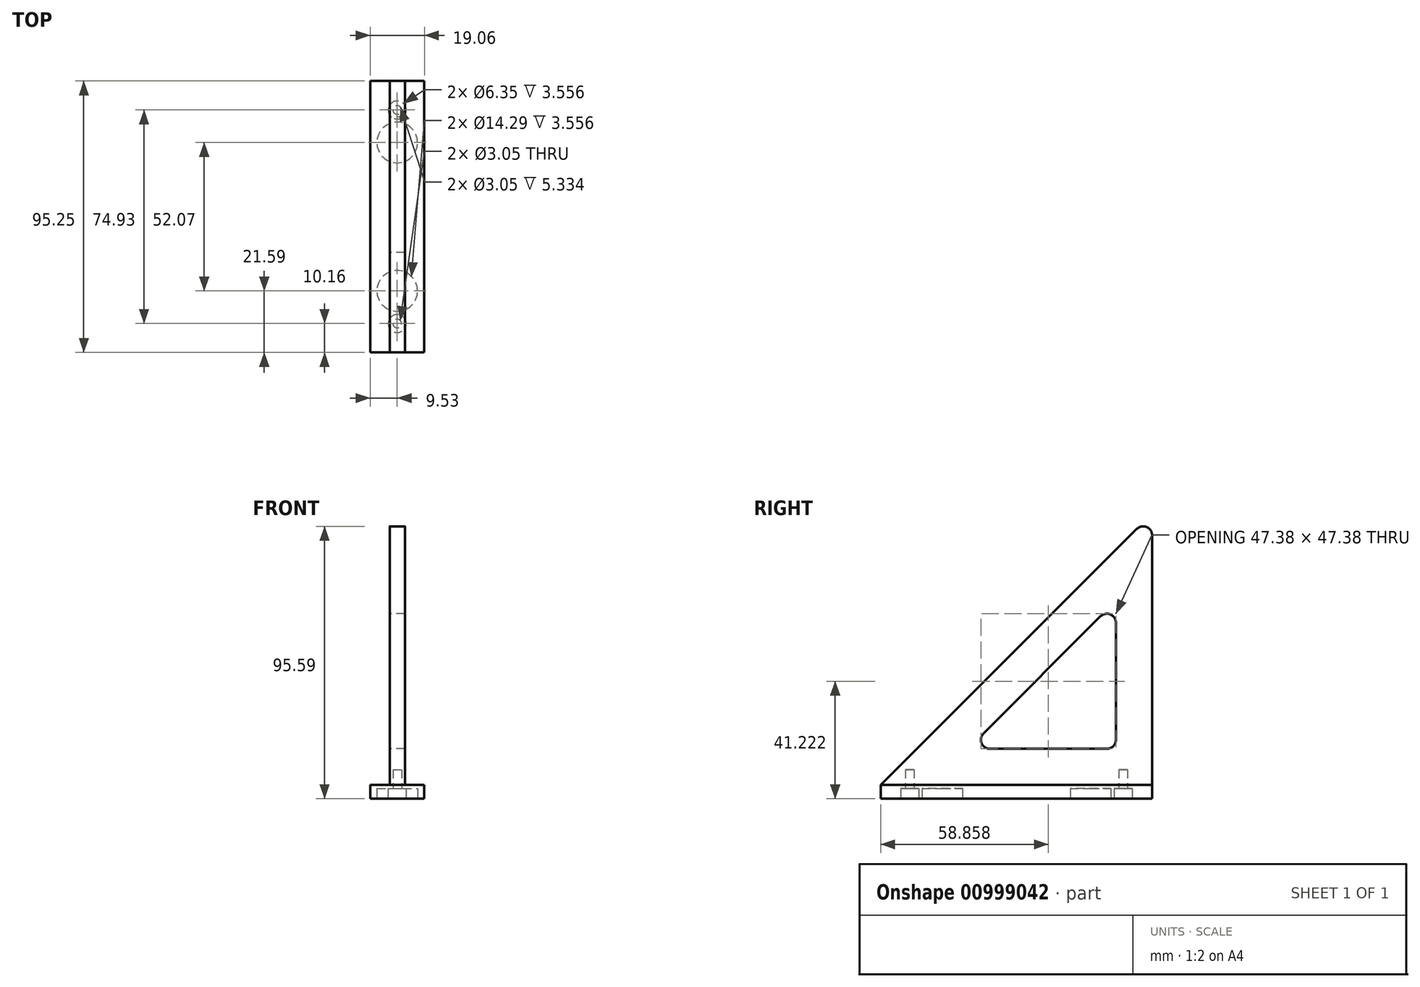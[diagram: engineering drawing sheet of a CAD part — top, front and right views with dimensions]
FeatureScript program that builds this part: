
annotation { "Feature Type Name" : "Feature", "Feature Type Description" : "" }
export const myFeature = defineFeature(function(context is Context, id is Id, definition is map)
    precondition{}
    {
        {
            var Q0;
            Q0=qCreatedBy(makeId("Right.planeOp"),FACE);
            var sketch = newSketch(context, id + "F0", { "sketchPlane" : qUnion([Q0])});
            skLineSegment(sketch, "E0", {"start": v(0, 0) * mm, "end": v(89.83, 89.83) * mm});
            skLineSegment(sketch, "E1", {"start": v(95.25, 87.58) * mm, "end": v(95.25, 0) * mm});
            skLineSegment(sketch, "E2", {"start": v(95.25, 0) * mm, "end": v(7.67, 0) * mm});
            skLineSegment(sketch, "E3.0", {"start": v(36.08, 18.12) * mm, "end": v(77.13, 59.17) * mm});
            skLineSegment(sketch, "E3.1", {"start": v(79.38, 12.7) * mm, "end": v(38.33, 12.7) * mm});
            skLineSegment(sketch, "E3.2", {"start": v(82.55, 56.92) * mm, "end": v(82.55, 15.88) * mm});
            skPoint(sketch, "E4.visualSharp", {"position": v(95.25, 95.25) * mm});
            skArc(sketch, "E4.filletArc", {"start": v(95.25, 87.58) * mm, "mid": v(93.3, 90.52) * mm, "end": v(89.83, 89.83) * mm});
            skPoint(sketch, "E5.visualSharp", {"position": v(0, 0) * mm});
            skPoint(sketch, "E6.visualSharp", {"position": v(30.66, 12.7) * mm});
            skArc(sketch, "E6.filletArc", {"start": v(36.08, 18.12) * mm, "mid": v(35.4, 14.66) * mm, "end": v(38.33, 12.7) * mm});
            skPoint(sketch, "E7.visualSharp", {"position": v(82.55, 64.59) * mm});
            skArc(sketch, "E7.filletArc", {"start": v(82.55, 56.92) * mm, "mid": v(80.6, 59.86) * mm, "end": v(77.13, 59.17) * mm});
            skPoint(sketch, "E8.visualSharp", {"position": v(82.55, 12.7) * mm});
            skArc(sketch, "E8.filletArc", {"start": v(79.38, 12.7) * mm, "mid": v(81.62, 13.63) * mm, "end": v(82.55, 15.88) * mm});
            skLineSegment(sketch, "E9", {"start": v(0, 0) * mm, "end": v(7.67, 0) * mm});
            skPoint(sketch, "E10.visualSharp", {"position": v(24.47, 24.47) * mm});
            skSolve(sketch);
        }
        {
            var Q0;
            Q0=makeQuery(id+"F0.imprint","IMPRINT",FACE,{"disambiguationData":[TD([[makeQuery(id+"F0.imprint","IMPRINT",EDGE,{"derivedFrom":sQuery(id+"F0.wireOp",EDGE,"E0")}),-1.0]])]});
            extrude(context, id + "F1", {"entities" : qUnion([Q0]), "depth" : 2.67 * mm, "offsetDistance" : 25.4 * mm, "hasSecondDirection" : true, "secondDirectionOppositeDirection" : true, "secondDirectionDepth" : 2.67 * mm});
        }
        {
            var Q0;
            Q0=qCreatedBy(makeId("Right.planeOp"),FACE);
            var sketch = newSketch(context, id + "F2", { "sketchPlane" : qUnion([Q0])});
            skLineSegment(sketch, "E11.bottom", {"start": v(95.25, 0) * mm, "end": v(0, 0) * mm});
            skLineSegment(sketch, "E11.top", {"start": v(95.25, -4.83) * mm, "end": v(0, -4.83) * mm});
            skLineSegment(sketch, "E11.left", {"start": v(95.25, -4.83) * mm, "end": v(95.25, 0) * mm});
            skLineSegment(sketch, "E11.right", {"start": v(0, -4.83) * mm, "end": v(0, 0) * mm});
            skSolve(sketch);
        }
        {
            var Q0;
            Q0 = qSketchRegion(id + "F2", true);
            extrude(context, id + "F3", {"entities" : qUnion([Q0]), "depth" : 9.52 * mm, "offsetDistance" : 25.4 * mm, "hasSecondDirection" : true, "secondDirectionOppositeDirection" : true, "secondDirectionDepth" : 9.52 * mm});
        }
        {
            var Q0;
            Q0=makeQuery(id+"F3.opExtrude","SWEPT_FACE",FACE,{"disambiguationData":[OSD([sQuery(id+"F2.wireOp",EDGE,"E11.top")])]});
            var sketch = newSketch(context, id + "F4", { "sketchPlane" : qUnion([Q0])});
            skCircle(sketch, "E12", {"center": v(0, -85.1) * mm, "radius": 3.18 * mm});
            skCircle(sketch, "E13", {"center": v(0, -10.16) * mm, "radius": 3.18 * mm});
            skCircle(sketch, "E14", {"center": v(0, -73.66) * mm, "radius": 7.14 * mm});
            skCircle(sketch, "E15", {"center": v(0, -21.59) * mm, "radius": 7.14 * mm});
            skSolve(sketch);
        }
        {
            var Q0;
            Q0 = qSketchRegion(id + "F4", true);
            extrude(context, id + "F5", {"entities" : qUnion([Q0]), "operationType" : NewBodyOperationType.REMOVE, "oppositeDirection" : true, "depth" : 3.56 * mm, "offsetDistance" : 25.4 * mm});
        }
        {
            var Q0;
            Q0=makeQuery(id+"F3.opExtrude","SWEPT_FACE",FACE,{"disambiguationData":[OSD([sQuery(id+"F2.wireOp",EDGE,"E11.top")])]});
            var sketch = newSketch(context, id + "F6", { "sketchPlane" : qUnion([Q0])});
            skCircle(sketch, "E16", {"center": v(0, -85.1) * mm, "radius": 1.52 * mm});
            skCircle(sketch, "E17", {"center": v(0, -10.16) * mm, "radius": 1.52 * mm});
            skSolve(sketch);
        }
        {
            var Q0;
            Q0 = qSketchRegion(id + "F6", true);
            extrude(context, id + "F7", {"entities" : qUnion([Q0]), "operationType" : NewBodyOperationType.REMOVE, "oppositeDirection" : true, "depth" : 10.16 * mm, "offsetDistance" : 25.4 * mm});
        }
    });
